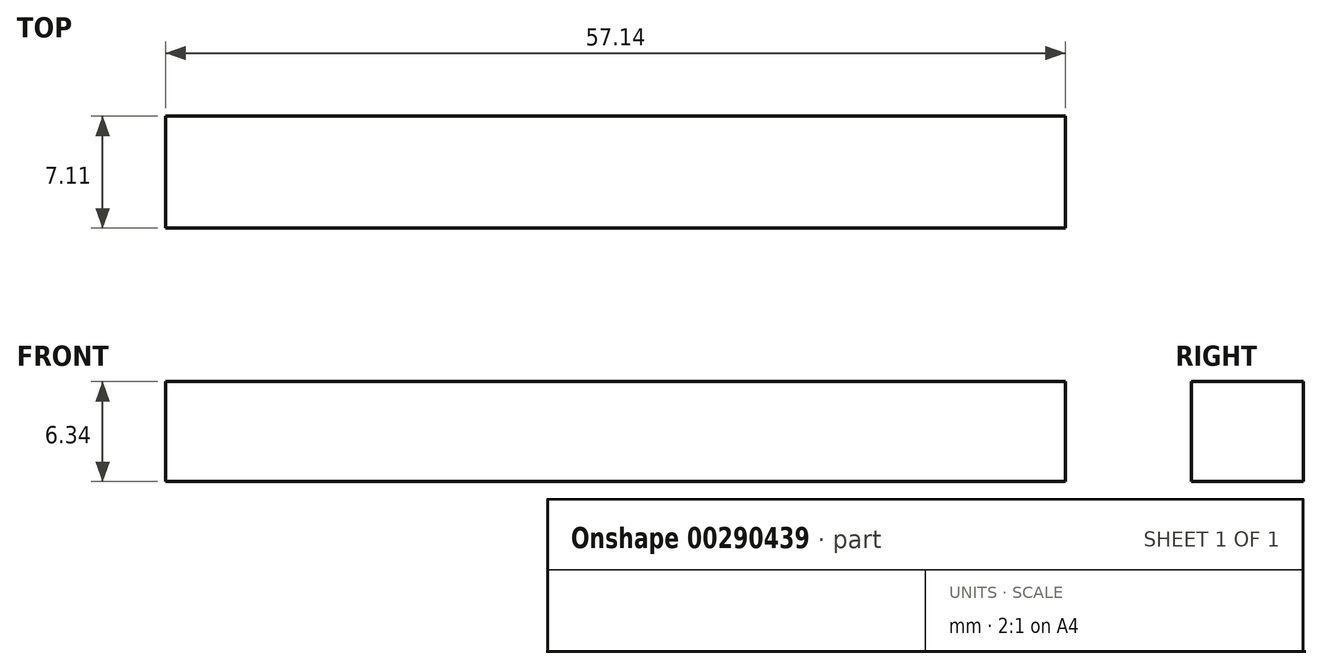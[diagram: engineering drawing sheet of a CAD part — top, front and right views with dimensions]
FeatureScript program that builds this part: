
annotation { "Feature Type Name" : "Feature", "Feature Type Description" : "" }
export const myFeature = defineFeature(function(context is Context, id is Id, definition is map)
    precondition{}
    {
        {
            var Q0;
            Q0=qCreatedBy(makeId("Front.planeOp"),FACE);
            var sketch = newSketch(context, id + "F0", { "sketchPlane" : qUnion([Q0])});
            skLineSegment(sketch, "E0", {"start": v(0, 3.18) * mm, "end": v(28.57, 3.18) * mm});
            skLineSegment(sketch, "E1", {"start": v(28.58, 3.17) * mm, "end": v(28.58, 0) * mm});
            skLineSegment(sketch, "E2.MirrorCS", {"start": v(0, -3.18) * mm, "end": v(28.58, -3.18) * mm});
            skLineSegment(sketch, "E3.MirrorCS", {"start": v(28.58, -3.18) * mm, "end": v(28.58, 0) * mm});
            skLineSegment(sketch, "E4.MirrorCS", {"start": v(-28.58, 3.18) * mm, "end": v(-28.58, 0) * mm});
            skLineSegment(sketch, "E5.MirrorCS", {"start": v(0, -3.17) * mm, "end": v(-28.58, -3.18) * mm});
            skLineSegment(sketch, "E6.MirrorCS", {"start": v(-28.58, -3.18) * mm, "end": v(-28.58, 0) * mm});
            skLineSegment(sketch, "E7.MirrorCS", {"start": v(0, 3.18) * mm, "end": v(-28.58, 3.17) * mm});
            skSolve(sketch);
        }
        {
            var Q0;
            Q0 = qSketchRegion(id + "F0", true);
            extrude(context, id + "F1", {"entities" : qUnion([Q0]), "depth" : 7.11 * mm});
        }
    });
